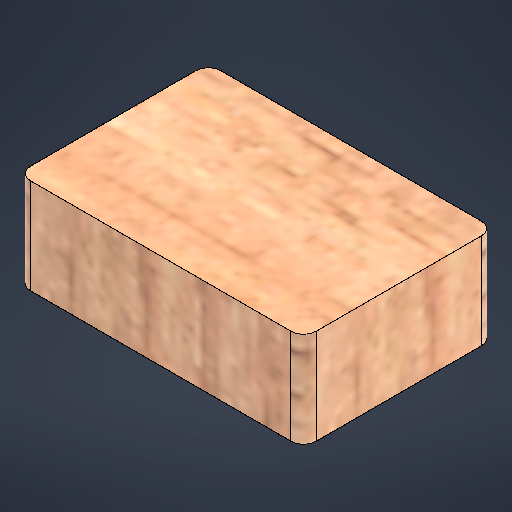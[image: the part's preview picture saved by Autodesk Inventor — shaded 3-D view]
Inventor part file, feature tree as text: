
AUTODESK INVENTOR PART (.ipt)
format: ipt  version: 2025.3 (Build 293356000, 356)  size: 359,424 bytes
history: native  units: mm
features: extrude x1, fillet x1, sketch x1
ambient origin geometry x8: Origin, YZ Plane, XZ Plane, XY Plane, X Axis, Y Axis, Z Axis, Center Point
bodies: Solid1 (feature_tree)
feature tree (3):
  extrude  "Extrusion1"  Depth=30.0mm
  fillet  "Fillet1"  Radius=15.0mm
  sketch  "Sketch1"  dims[d0=45.0mm d1=30.0mm d2=15.0mm d3=0.0mm d4=2.0mm]
